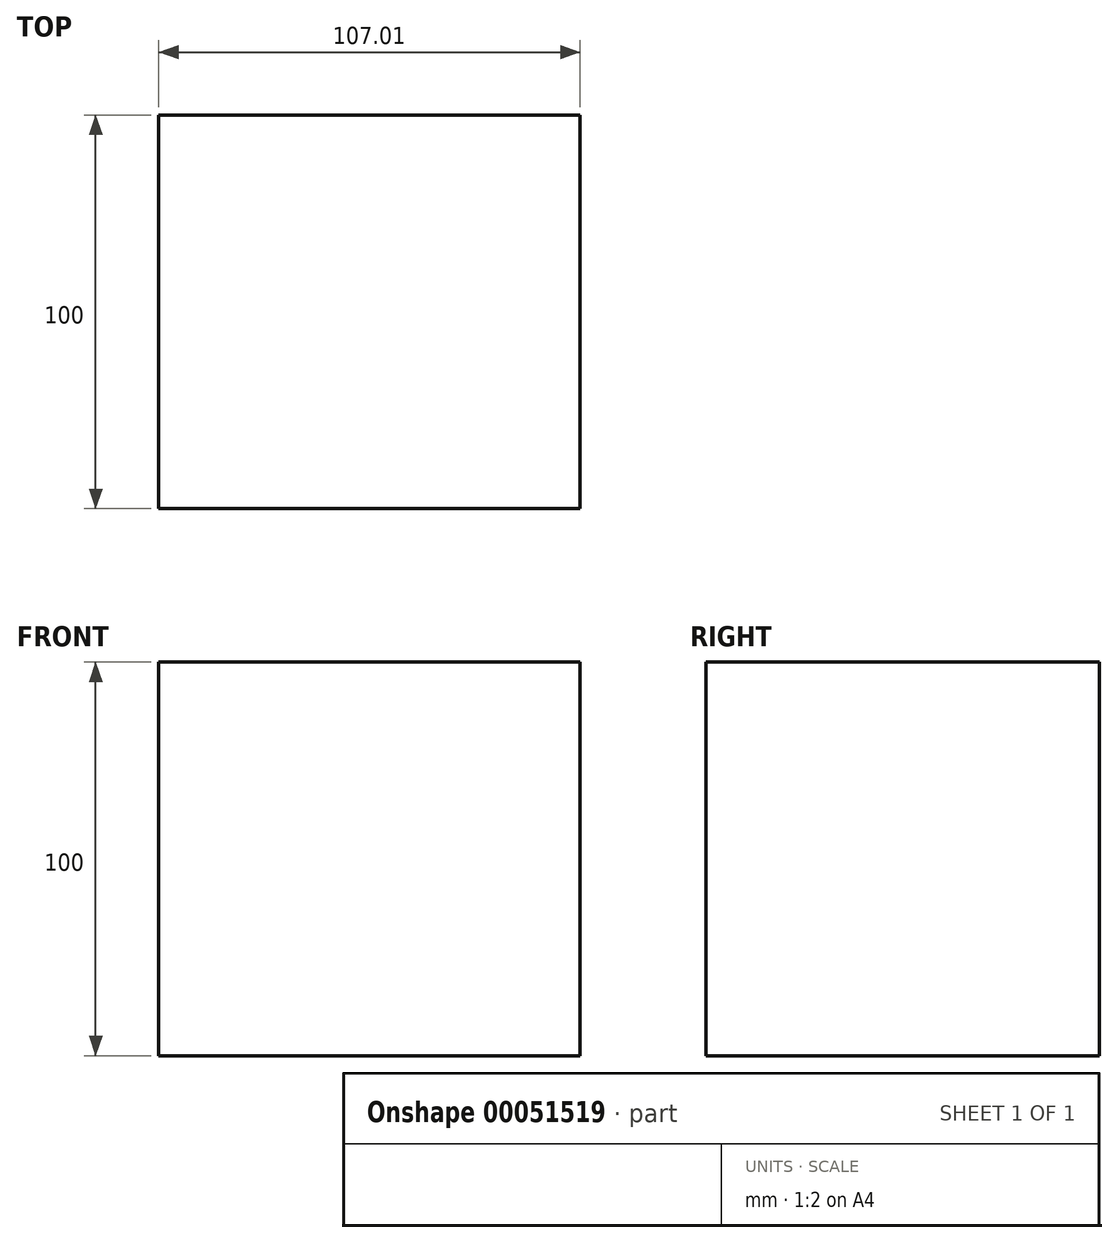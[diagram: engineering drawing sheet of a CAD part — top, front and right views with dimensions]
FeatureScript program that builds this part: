
annotation { "Feature Type Name" : "Feature", "Feature Type Description" : "" }
export const myFeature = defineFeature(function(context is Context, id is Id, definition is map)
    precondition{}
    {
        {
            var Q0;
            Q0=qCreatedBy(makeId("Top.planeOp"),FACE);
            var sketch = newSketch(context, id + "F0", { "sketchPlane" : qUnion([Q0])});
            skLineSegment(sketch, "E0.bottom", {"start": v(-51.38, 50) * mm, "end": v(55.63, 50) * mm});
            skLineSegment(sketch, "E0.top", {"start": v(-51.38, -50) * mm, "end": v(55.63, -50) * mm});
            skLineSegment(sketch, "E0.left", {"start": v(-51.38, 50) * mm, "end": v(-51.38, -50) * mm});
            skLineSegment(sketch, "E0.right", {"start": v(55.63, 50) * mm, "end": v(55.63, -50) * mm});
            skSolve(sketch);
        }
        {
            var Q0;
            Q0 = qSketchRegion(id + "F0", true);
            extrude(context, id + "F1", {"entities" : qUnion([Q0]), "depth" : 100 * mm});
        }
    });
